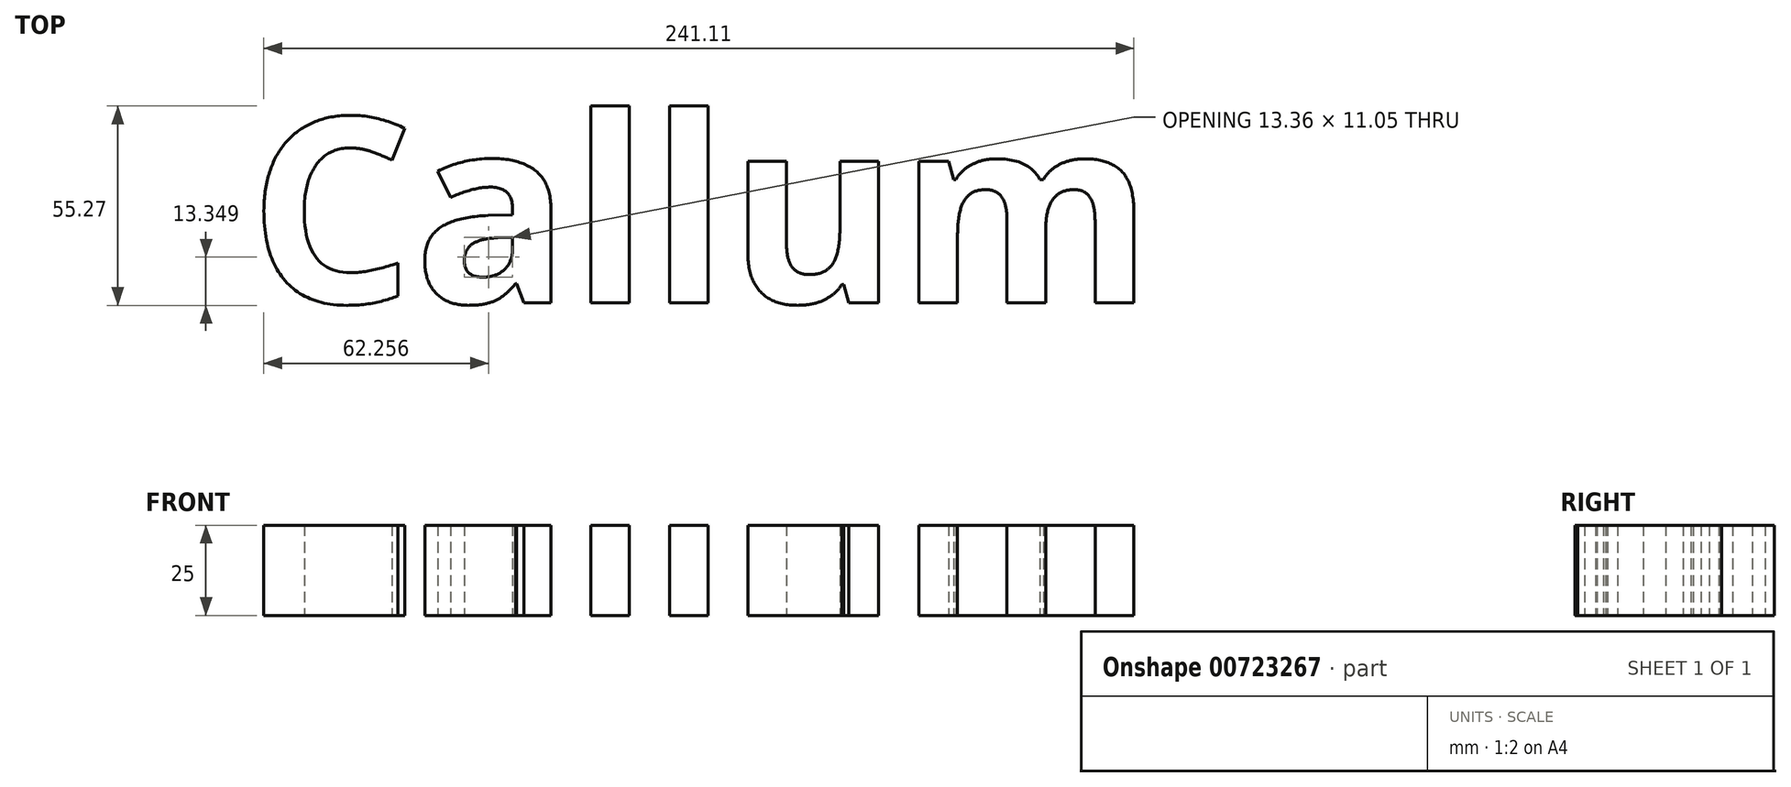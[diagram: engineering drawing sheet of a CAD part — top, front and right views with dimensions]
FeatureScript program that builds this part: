
annotation { "Feature Type Name" : "Feature", "Feature Type Description" : "" }
export const myFeature = defineFeature(function(context is Context, id is Id, definition is map)
    precondition{}
    {
        {
            var Q0;
            Q0=qCreatedBy(makeId("Top.planeOp"),FACE);
            var sketch = newSketch(context, id + "F0", { "sketchPlane" : qUnion([Q0])});
            skText(sketch, "E0", { "text": "Callum ", "fontName": "OpenSans-Bold.ttf"});
            const initialGuessF0  = {"E0": [-0.13133, -0.02951, 1, 0, 0.0517]};
            skSetInitialGuess(sketch, initialGuessF0);
            skSolve(sketch);
        }
        {
            var Q0;
            Q0 = qSketchRegion(id + "F0", true);
            extrude(context, id + "F1", {"entities" : qUnion([Q0]), "depth" : 25 * mm, "offsetDistance" : 25 * mm});
        }
    });
